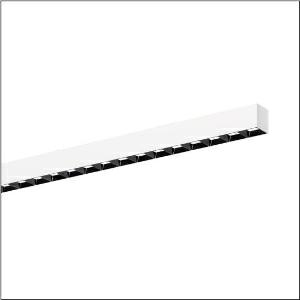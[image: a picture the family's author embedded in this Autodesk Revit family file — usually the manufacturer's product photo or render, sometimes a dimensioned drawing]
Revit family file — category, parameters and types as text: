
# Revit family: silica_r__21_51mx22da44wb_17fd
name_source: partatom
category: Lighting Fixtures
units: mm (PartAtom-declared; Revit-internal decimal feet)

## family parameters
Cut with Voids When Loaded = No
Host = Face
Light Source = No
Part Type = Normal
Room Calculation Point = No
Round Connector Dimension = Use Diameter
Shared = No

## types (1)
- --- (1 x LED, 4320 lm, 25.6 W, 4000K)
    Apparent Load = 26 VA
    CIE Flux Codes = 86 100 100 100 100
    Color Rendering = 80
    Color Temperature = 4000K
    Default Elevation = 1800 mm
    Description = Silica® 21, office luminaire, primary light control with darklight reflector, of PMMA, black, CAT 2 (L<= 3000cd/m²), light emission: direct distribution, primary light characteristic: symmetric, installation type: surface-mounted, LED, rated luminous flux: 4.320lm, luminous efficacy: 169lm/W, light colour: 840, colour temperature: 4000K, with terminal, 3+2-pole, max. 2.5mm², mains connection: 220..240V, AC, 50/60Hz, rated input power: 25.6W, luminaire housing, of aluminium, traffic white (RAL 9016), length: 1.204mm, width: 53mm, height: 53mm, protection rating (complete): IP20, insulation class (complete): insulation class I (protective earthing), certification: CE, permissible operating ambient temperature: 0..+35°C, standard: EN 50419, packaging unit: 1 piece
    Height = 0 mm  [stored 0 ft]
    Lamp = 1 x LED
    Lamp Light Flux = 4320 lm
    Lamp Power = 25.6 W
    Lamp count = 1
    Length = 1204 mm
    Luminous efficacy = 169 lm/W
    Manufacturer = Siteco
    ModVariant = No
    Model = 51MX22DA44WB
    Mounting Place = Ceiling
    Mounting Type = Recessed
    Number of Poles = 1
    OnlyDefault = Yes
    Power Factor = 1
    Product Name = Silica® 21
    Product group = office luminaire | ceiling recessed
    ProductGroupID = 400
    Protection Class = Protection class I
    Protection Degree = IP 20
    RLX_Detail_Level = 1
    RLX_Emergency_Light_Flux = 0 lm
    RLX_Emergency_Type = 0
    RLX_Emergency_Type_DB = No
    RlxData = <blob elided: 41285 chars, md5=b29d6afc>
    Socket = socket
    Standby Power = 0 W
    System Light Flux = 4320 lm
    System Power = 26 W
    Type Comments = factory setting: luminous flux: 100 % | dim-lin: 254 | 367 mA
    Type Image = l_1335873.jpg
    URL = http://relux.com
    VarID = @adj_095309
    Voltage = 0 V
    Weight = 0.00 kg
    Width = 53 mm

note: [stored X ft] marks values corroborated as IEEE doubles in the binary element streams (Revit-internal decimal feet)

## geometry (parser evidence)
native form markers: Blend x4, Sweep x11
no freeform markers — native parametric forms only
